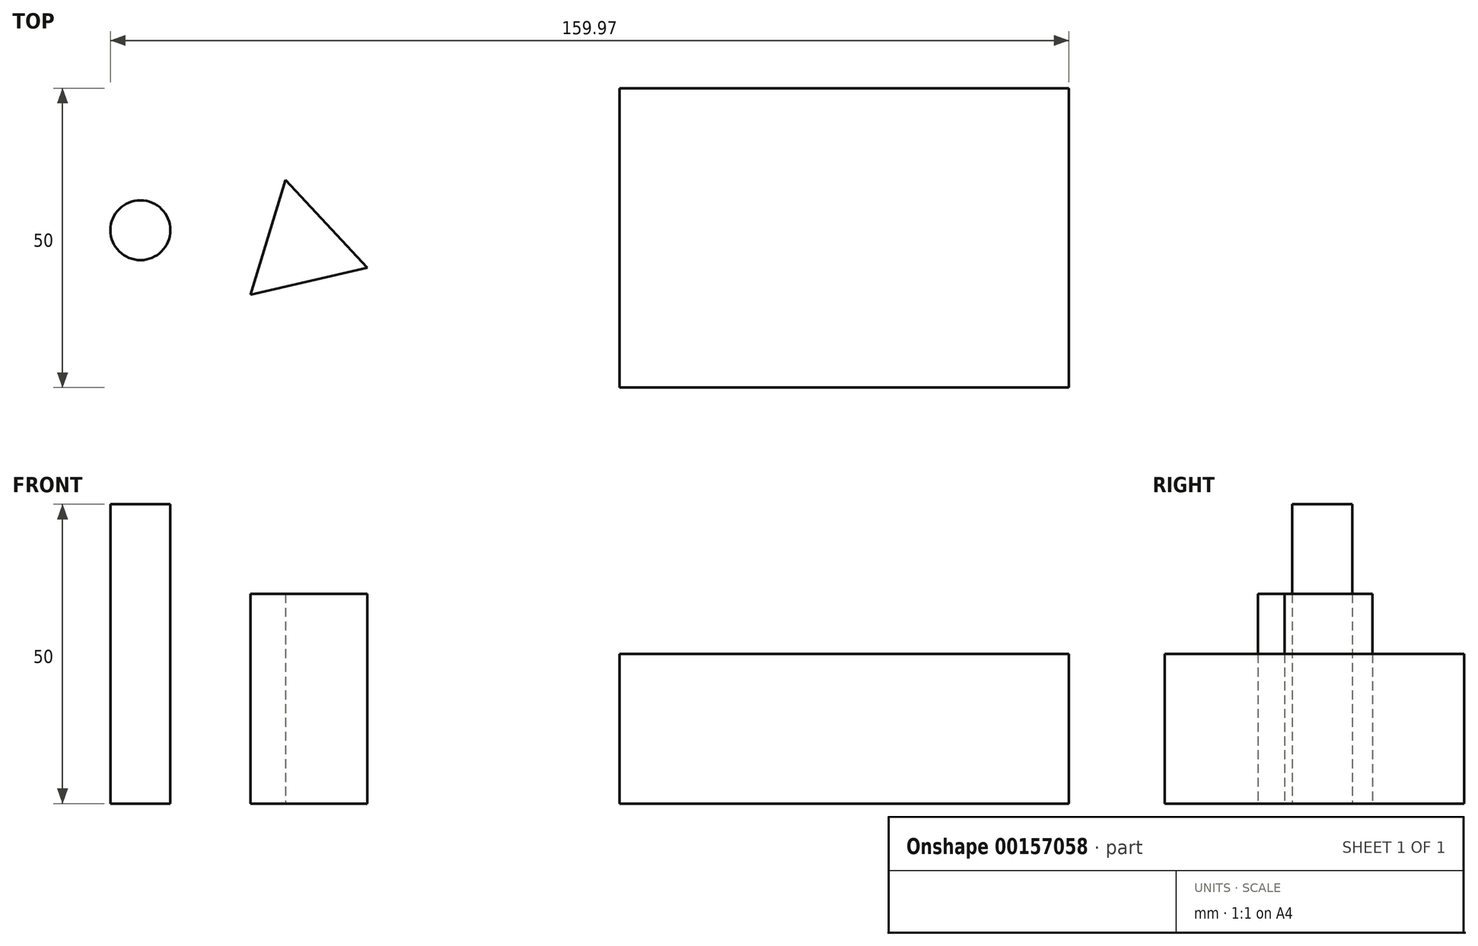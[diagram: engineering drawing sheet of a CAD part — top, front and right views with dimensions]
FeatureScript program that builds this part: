
annotation { "Feature Type Name" : "Feature", "Feature Type Description" : "" }
export const myFeature = defineFeature(function(context is Context, id is Id, definition is map)
    precondition{}
    {
        {
            var Q0;
            Q0=qCreatedBy(makeId("Top.planeOp"),FACE);
            var sketch = newSketch(context, id + "F0", { "sketchPlane" : qUnion([Q0])});
            skLineSegment(sketch, "E0.bottom", {"start": v(-39.69, -34.65) * mm, "end": v(35.31, -34.65) * mm});
            skLineSegment(sketch, "E0.top", {"start": v(-39.69, 15.35) * mm, "end": v(35.31, 15.35) * mm});
            skLineSegment(sketch, "E0.left", {"start": v(-39.69, -34.65) * mm, "end": v(-39.69, 15.35) * mm});
            skLineSegment(sketch, "E0.right", {"start": v(35.31, -34.65) * mm, "end": v(35.31, 15.35) * mm});
            skSolve(sketch);
        }
        {
            var Q0;
            Q0=makeQuery(id+"F0.imprint","IMPRINT",FACE,{"disambiguationData":[TD([[makeQuery(id+"F0.imprint","IMPRINT",EDGE,{"derivedFrom":sQuery(id+"F0.wireOp",EDGE,"E0.bottom")}),1.0]])]});
            extrude(context, id + "F1", {"entities" : qUnion([Q0]), "depth" : 25 * mm});
        }
        {
            var Q0;
            Q0=qCreatedBy(makeId("Top.planeOp"),FACE);
            var sketch = newSketch(context, id + "F2", { "sketchPlane" : qUnion([Q0])});
            skCircle(sketch, "E1", {"center": v(-119.66, -8.37) * mm, "radius": 5 * mm});
            skSolve(sketch);
        }
        {
            var Q0;
            Q0=makeQuery(id+"F2.imprint","IMPRINT",FACE,{"disambiguationData":[TD([[makeQuery(id+"F2.imprint","IMPRINT",EDGE,{"derivedFrom":sQuery(id+"F2.wireOp",EDGE,"E1")}),1.0]])]});
            extrude(context, id + "F3", {"entities" : qUnion([Q0]), "depth" : 50 * mm});
        }
        {
            var Q0;
            Q0=qCreatedBy(makeId("Top.planeOp"),FACE);
            var sketch = newSketch(context, id + "F4", { "sketchPlane" : qUnion([Q0])});
            skLineSegment(sketch, "E2", {"start": v(-101.3, -19.12) * mm, "end": v(-95.45, 0) * mm});
            skLineSegment(sketch, "E3", {"start": v(-95.45, 0) * mm, "end": v(-81.82, -14.64) * mm});
            skLineSegment(sketch, "E4", {"start": v(-81.82, -14.64) * mm, "end": v(-101.3, -19.12) * mm});
            skSolve(sketch);
        }
        {
            var Q0;
            Q0=makeQuery(id+"F4.imprint","IMPRINT",FACE,{"disambiguationData":[TD([[makeQuery(id+"F4.imprint","IMPRINT",EDGE,{"derivedFrom":sQuery(id+"F4.wireOp",EDGE,"E2")}),-1.0]])]});
            extrude(context, id + "F5", {"entities" : qUnion([Q0]), "depth" : 35 * mm});
        }
    });
